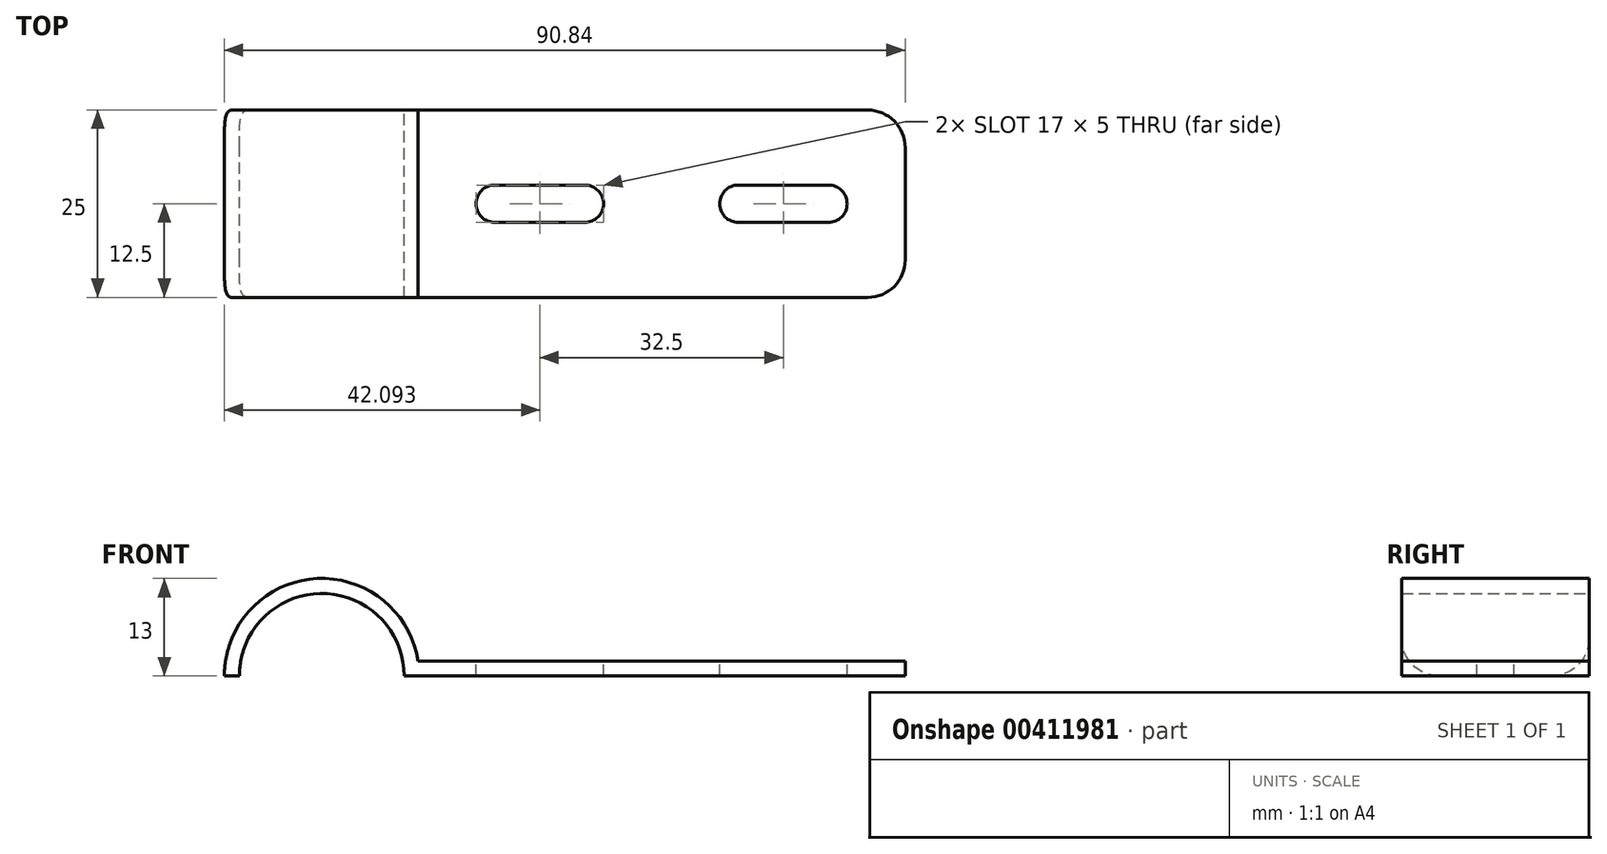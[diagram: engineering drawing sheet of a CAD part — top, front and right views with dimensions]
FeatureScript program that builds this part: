
annotation { "Feature Type Name" : "Feature", "Feature Type Description" : "" }
export const myFeature = defineFeature(function(context is Context, id is Id, definition is map)
    precondition{}
    {
        {
            var Q0;
            Q0=qCreatedBy(makeId("Front.planeOp"),FACE);
            var sketch = newSketch(context, id + "F0", { "sketchPlane" : qUnion([Q0])});
            skLineSegment(sketch, "E0", {"start": v(33.42, 0) * mm, "end": v(-33.42, 0) * mm});
            skArc(sketch, "E1", {"start": v(-33.42, 0) * mm, "mid": v(-44.42, 11) * mm, "end": v(-55.42, 0) * mm});
            skArc(sketch, "E2.0", {"start": v(-31.58, 2) * mm, "mid": v(-45.43, 12.96) * mm, "end": v(-57.42, 0) * mm});
            skLineSegment(sketch, "E2.1", {"start": v(33.42, 2) * mm, "end": v(-31.58, 2) * mm});
            skLineSegment(sketch, "E3", {"start": v(33.42, 2) * mm, "end": v(33.42, 0) * mm});
            skLineSegment(sketch, "E4", {"start": v(-55.42, 0) * mm, "end": v(-57.42, 0) * mm});
            skSolve(sketch);
        }
        {
            var Q0;
            Q0=makeQuery(id+"F0.imprint","IMPRINT",FACE,{"disambiguationData":[TD([[makeQuery(id+"F0.imprint","IMPRINT",EDGE,{"derivedFrom":sQuery(id+"F0.wireOp",EDGE,"E0")}),-1.0]])]});
            extrude(context, id + "F1", {"entities" : qUnion([Q0]), "depth" : 25 * mm, "offsetDistance" : 25 * mm, "symmetric" : true});
        }
        {
            var Q0;
            Q0=makeQuery(id+"F1.opExtrude","SWEPT_FACE",FACE,{"disambiguationData":[OSD([sQuery(id+"F0.wireOp",EDGE,"E2.1")])]});
            var sketch = newSketch(context, id + "F2", { "sketchPlane" : qUnion([Q0])});
            skPoint(sketch, "E5", {"position": v(0.92, 12.5) * mm});
            skPoint(sketch, "E6", {"position": v(33.42, 12.5) * mm});
            skPoint(sketch, "E7", {"position": v(0.92, -12.5) * mm});
            skPoint(sketch, "E8", {"position": v(33.42, -12.5) * mm});
            skLineSegment(sketch, "E9", {"start": v(0.92, 12.5) * mm, "end": v(0.92, -12.5) * mm});
            skPoint(sketch, "E10", {"position": v(17.17, 12.5) * mm});
            skLineSegment(sketch, "E11", {"start": v(17.17, 12.5) * mm, "end": v(17.17, -12.5) * mm, "construction": true});
            skLineSegment(sketch, "E12", {"start": v(0.92, 0) * mm, "end": v(33.42, 0) * mm, "construction": true});
            skPoint(sketch, "E13", {"position": v(17.17, 0) * mm});
            skArc(sketch, "E14", {"start": v(11.17, 2.5) * mm, "mid": v(8.67, 0) * mm, "end": v(11.17, -2.5) * mm});
            skArc(sketch, "E15", {"start": v(23.17, -2.5) * mm, "mid": v(25.67, 0) * mm, "end": v(23.17, 2.5) * mm});
            skLineSegment(sketch, "E16", {"start": v(11.17, 2.5) * mm, "end": v(23.17, 2.5) * mm});
            skLineSegment(sketch, "E17", {"start": v(11.17, -2.5) * mm, "end": v(23.17, -2.5) * mm});
            skPoint(sketch, "E18", {"position": v(17.17, 2.5) * mm});
            skPoint(sketch, "E19", {"position": v(17.17, -2.5) * mm});
            skLineSegment(sketch, "E20", {"start": v(17.17, 2.5) * mm, "end": v(17.17, -2.5) * mm});
            skLineSegment(sketch, "E21.MirrorCS", {"start": v(-9.33, 2.5) * mm, "end": v(-21.33, 2.5) * mm});
            skArc(sketch, "E22.MirrorCS", {"start": v(-9.33, 2.5) * mm, "mid": v(-6.83, 0) * mm, "end": v(-9.33, -2.5) * mm});
            skLineSegment(sketch, "E23.MirrorCS", {"start": v(-9.33, -2.5) * mm, "end": v(-21.33, -2.5) * mm});
            skArc(sketch, "E24.MirrorCS", {"start": v(-21.33, -2.5) * mm, "mid": v(-23.83, 0) * mm, "end": v(-21.33, 2.5) * mm});
            skSolve(sketch);
        }
        {
            var Q0;
            {var subQ0=sQuery(id+"F2.wireOp",EDGE,"E14");Q0=makeQuery(id+"F2.imprint","IMPRINT",FACE,{"disambiguationData":[TD([[makeQuery(id+"F2.imprint","IMPRINT",EDGE,{"derivedFrom":subQ0}),1.0]])]});}
            var Q1;
            {var subQ0=sQuery(id+"F2.wireOp",EDGE,"E15");Q1=makeQuery(id+"F2.imprint","IMPRINT",FACE,{"disambiguationData":[TD([[makeQuery(id+"F2.imprint","IMPRINT",EDGE,{"derivedFrom":subQ0}),1.0]])]});}
            var Q2;
            Q2=makeQuery(id+"F2.imprint","IMPRINT",FACE,{"disambiguationData":[TD([[makeQuery(id+"F2.imprint","IMPRINT",EDGE,{"derivedFrom":sQuery(id+"F2.wireOp",EDGE,"E21.MirrorCS")}),1.0]])]});
            extrude(context, id + "F3", {"entities" : qUnion([Q0, Q1, Q2]), "operationType" : NewBodyOperationType.REMOVE, "oppositeDirection" : true, "depth" : 25 * mm, "offsetDistance" : 25 * mm});
        }
        {
            var Q0;
            Q0=makeQuery(id+"F1.opExtrude","CAP_EDGE",EDGE,{"disambiguationData":[OSD([sQuery(id+"F0.wireOp",EDGE,"E3")])],"isStart":true});
            var Q1;
            Q1=makeQuery(id+"F1.opExtrude","CAP_EDGE",EDGE,{"disambiguationData":[OSD([sQuery(id+"F0.wireOp",EDGE,"E3")])],"isStart":false});
            var Q2;
            Q2=makeQuery(id+"F1.opExtrude","CAP_EDGE",EDGE,{"disambiguationData":[OSD([sQuery(id+"F0.wireOp",EDGE,"E4")])],"isStart":false});
            var Q3;
            Q3=makeQuery(id+"F1.opExtrude","CAP_EDGE",EDGE,{"disambiguationData":[OSD([sQuery(id+"F0.wireOp",EDGE,"E4")])],"isStart":true});
            fillet(context, id + "F4", {"entities" : qUnion([Q0, Q1, Q2, Q3]), "radius" : 5 * mm, "tangentPropagation" : true, "allowEdgeOverflow" : false});
        }
    });
